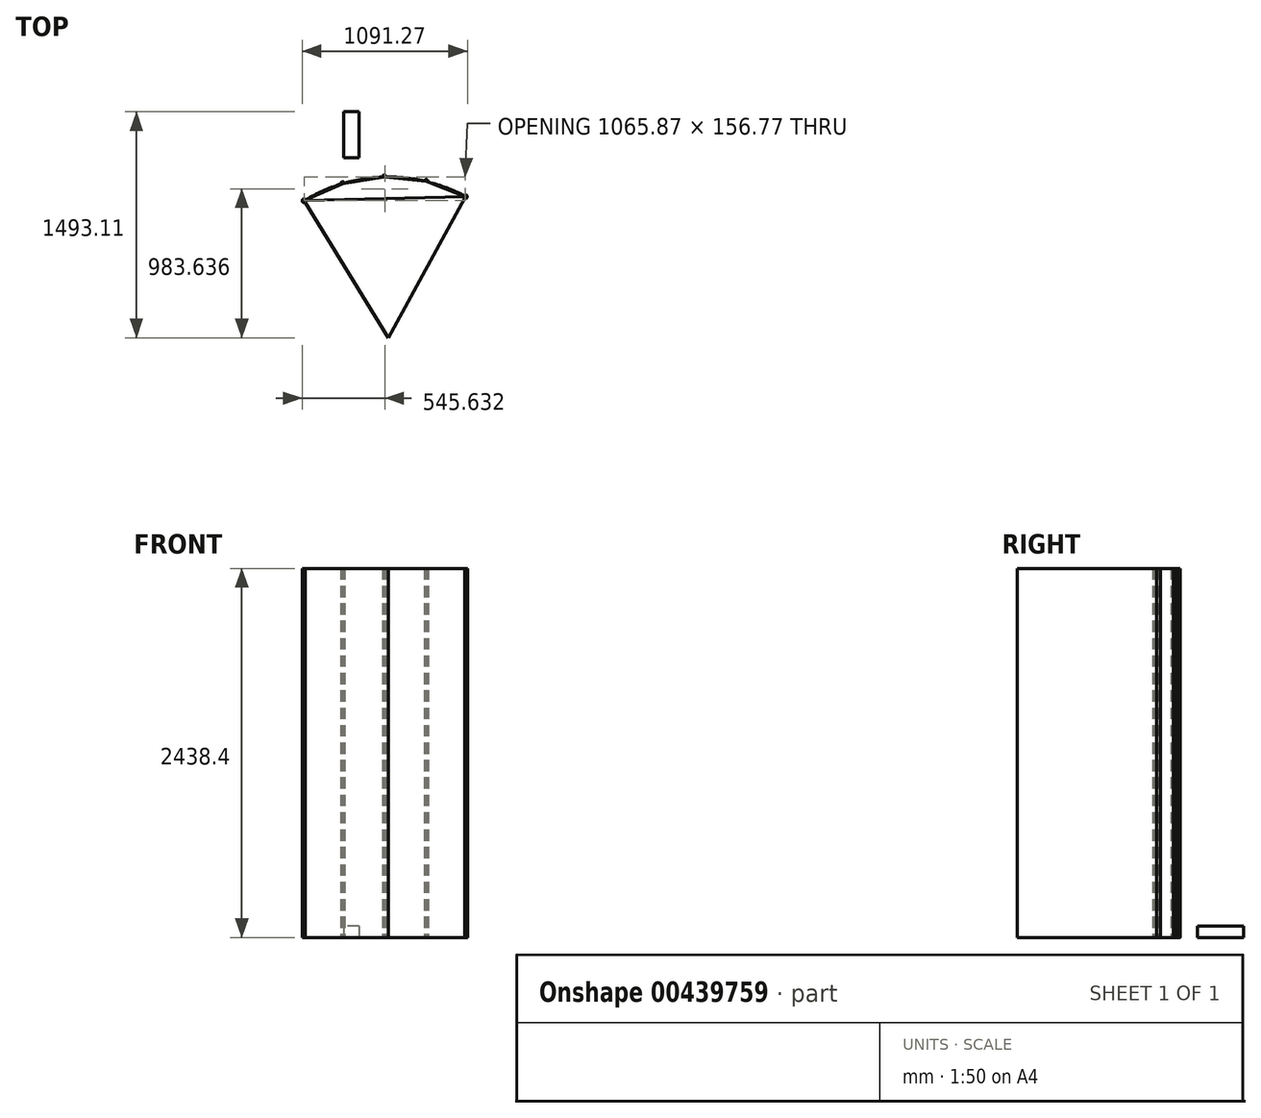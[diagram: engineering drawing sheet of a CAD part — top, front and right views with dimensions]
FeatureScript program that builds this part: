
annotation { "Feature Type Name" : "Feature", "Feature Type Description" : "" }
export const myFeature = defineFeature(function(context is Context, id is Id, definition is map)
    precondition{}
    {
        {
            var Q0;
            Q0=qCreatedBy(makeId("Top.planeOp"),FACE);
            var sketch = newSketch(context, id + "F0", { "sketchPlane" : qUnion([Q0])});
            skArc(sketch, "E0", {"start": v(-555.98, 905.25) * mm, "mid": v(-26.65, 1062.02) * mm, "end": v(509.89, 932) * mm});
            skLineSegment(sketch, "E1", {"start": v(-555.98, 905.25) * mm, "end": v(0, 0) * mm});
            skLineSegment(sketch, "E2", {"start": v(0, 0) * mm, "end": v(509.89, 932) * mm});
            skLineSegment(sketch, "E3", {"start": v(-26.33, 1049.32) * mm, "end": v(-26.65, 1062.02) * mm});
            skLineSegment(sketch, "E4", {"start": v(-555.98, 905.25) * mm, "end": v(509.89, 932) * mm});
            skPoint(sketch, "E5", {"position": v(-23.05, 918.62) * mm});
            skLineSegment(sketch, "E6", {"start": v(-555.98, 905.25) * mm, "end": v(-301.68, 1018.62) * mm});
            skLineSegment(sketch, "E7", {"start": v(-301.68, 1018.62) * mm, "end": v(-26.65, 1062.02) * mm});
            skPoint(sketch, "E8.end.orphan", {"position": v(-301.68, 911.63) * mm});
            skLineSegment(sketch, "E9", {"start": v(250.21, 1032.47) * mm, "end": v(-26.65, 1062.02) * mm});
            skLineSegment(sketch, "E10", {"start": v(509.89, 932) * mm, "end": v(250.21, 1032.47) * mm});
            skCircle(sketch, "E11", {"center": v(509.89, 932) * mm, "radius": 12.7 * mm});
            skCircle(sketch, "E12", {"center": v(250.21, 1032.47) * mm, "radius": 12.7 * mm});
            skCircle(sketch, "E13", {"center": v(-26.65, 1062.02) * mm, "radius": 12.7 * mm});
            skCircle(sketch, "E14", {"center": v(-301.68, 1018.62) * mm, "radius": 12.7 * mm});
            skCircle(sketch, "E15", {"center": v(-555.98, 905.25) * mm, "radius": 12.7 * mm});
            skLineSegment(sketch, "E16.trimOffspring", {"start": v(-298.07, 1006.44) * mm, "end": v(-301.68, 1018.62) * mm});
            skSolve(sketch);
        }
        {
            var Q0;
            {var subQ0=sQuery(id+"F0.wireOp",EDGE,"E2");Q0=makeQuery(id+"F0.imprint","IMPRINT",FACE,{"disambiguationData":[TD([[makeQuery(id+"F0.imprint","IMPRINT",EDGE,{"derivedFrom":subQ0}),1.0]])]});}
            var Q1;
            {var subQ0=sQuery(id+"F0.wireOp",EDGE,"E1");Q1=makeQuery(id+"F0.imprint","IMPRINT",FACE,{"disambiguationData":[TD([[makeQuery(id+"F0.imprint","IMPRINT",EDGE,{"derivedFrom":subQ0}),1.0]])]});}
            var Q2;
            Q2=qSketchRegion(id+"F0",true);
            extrude(context, id + "F1", {"entities" : qUnion([Q0, Q1, Q2]), "depth" : 2438.4 * mm});
        }
        {
            var Q0;
            Q0=qCreatedBy(makeId("Top.planeOp"),FACE);
            var sketch = newSketch(context, id + "F2", { "sketchPlane" : qUnion([Q0])});
            skLineSegment(sketch, "E17.bottom", {"start": v(-195.02, 1188.3) * mm, "end": v(-296.62, 1188.3) * mm});
            skLineSegment(sketch, "E17.top", {"start": v(-195.02, 1493.1) * mm, "end": v(-296.62, 1493.1) * mm});
            skLineSegment(sketch, "E17.left", {"start": v(-195.02, 1188.3) * mm, "end": v(-195.02, 1493.1) * mm});
            skLineSegment(sketch, "E17.right", {"start": v(-296.62, 1188.3) * mm, "end": v(-296.62, 1493.1) * mm});
            skSolve(sketch);
        }
        {
            var Q0;
            Q0=qSketchRegion(id+"F2",true);
            extrude(context, id + "F3", {"entities" : qUnion([Q0]), "depth" : 76.2 * mm});
        }
    });
